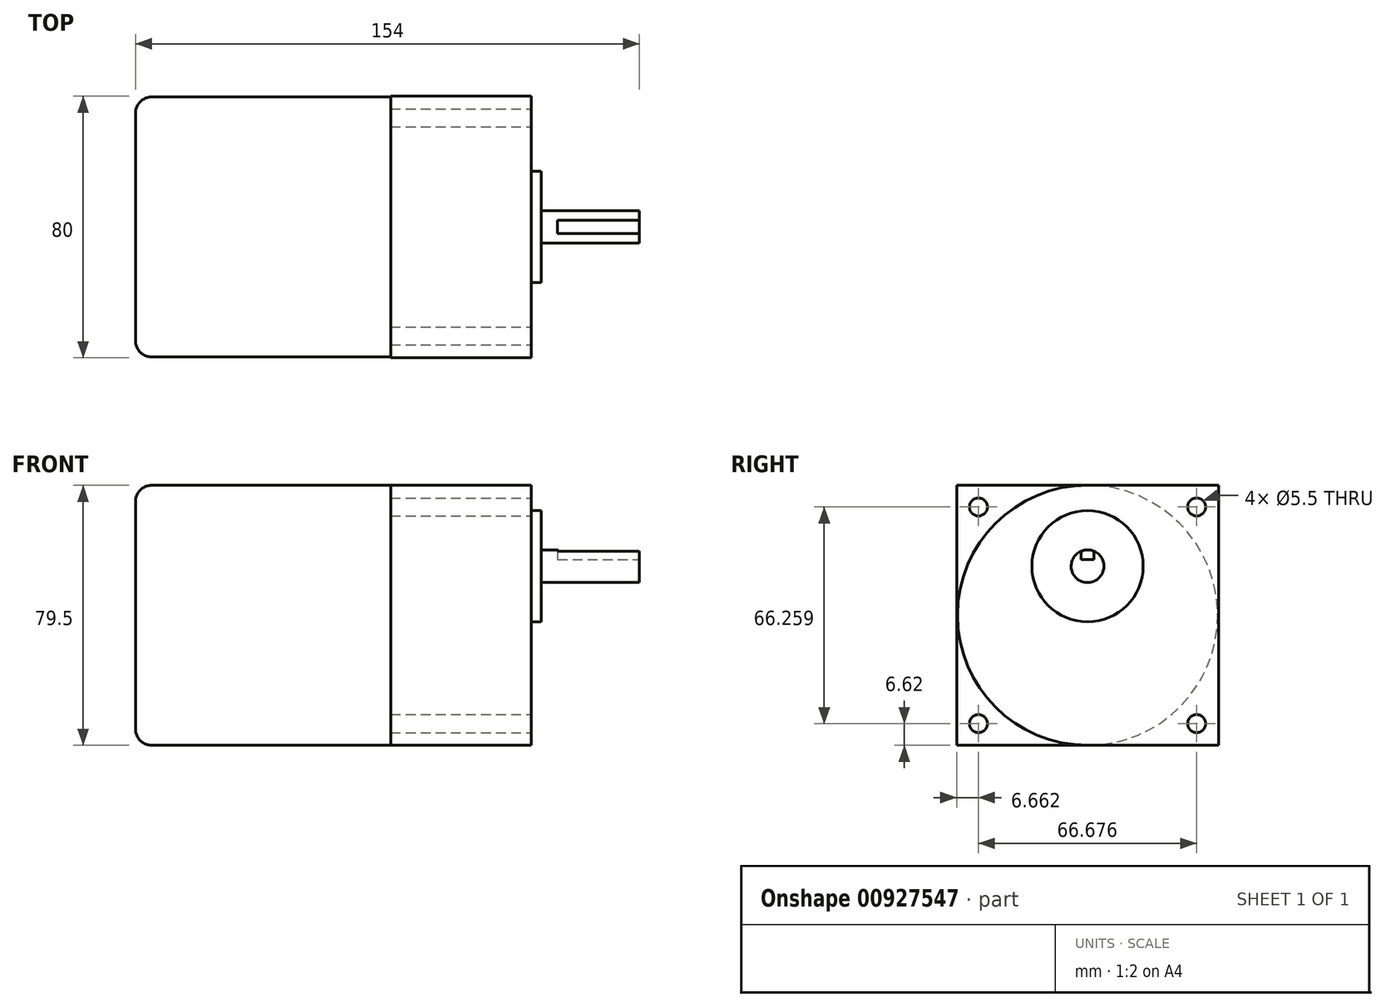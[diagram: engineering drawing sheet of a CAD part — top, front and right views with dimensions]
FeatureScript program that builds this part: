
annotation { "Feature Type Name" : "Feature", "Feature Type Description" : "" }
export const myFeature = defineFeature(function(context is Context, id is Id, definition is map)
    precondition{}
    {
        {
            var Q0;
            Q0=qCreatedBy(makeId("Right.planeOp"),FACE);
            var sketch = newSketch(context, id + "F0", { "sketchPlane" : qUnion([Q0])});
            skLineSegment(sketch, "E0.bottom", {"start": v(40, 39.75) * mm, "end": v(-40, 39.75) * mm});
            skLineSegment(sketch, "E0.top", {"start": v(40, -39.75) * mm, "end": v(-40, -39.75) * mm});
            skLineSegment(sketch, "E0.left", {"start": v(40, 39.75) * mm, "end": v(40, -39.75) * mm});
            skLineSegment(sketch, "E0.right", {"start": v(-40, 39.75) * mm, "end": v(-40, -39.75) * mm});
            skPoint(sketch, "E0.middle", {"position": v(0, 0) * mm});
            skSolve(sketch);
        }
        {
            var Q0;
            Q0 = qSketchRegion(id + "F0", true);
            extrude(context, id + "F1", {"entities" : qUnion([Q0]), "oppositeDirection" : true, "depth" : (9 + 34) * mm, "offsetDistance" : 25 * mm});
        }
        {
            var Q0;
            Q0=makeQuery(id+"F1.opExtrude","CAP_FACE",FACE,{"disambiguationData":[OSD([sQuery(id+"F0.wireOp",EDGE,"E0.bottom"),sQuery(id+"F0.wireOp",EDGE,"E0.top"),sQuery(id+"F0.wireOp",EDGE,"E0.left"),sQuery(id+"F0.wireOp",EDGE,"E0.right")])],"isStart":false});
            var sketch = newSketch(context, id + "F2", { "sketchPlane" : qUnion([Q0])});
            skCircle(sketch, "E1", {"center": v(0, 0) * mm, "radius": 39.75 * mm});
            skSolve(sketch);
        }
        {
            var Q0;
            {var subQ0=sQuery(id+"F2.wireOp",EDGE,"E1");var subQ1=makeQuery(id+"F2.imprint","INTERSECT",VERTEX,{"derivedFrom":[makeQuery(id+"F1.opExtrude","CAP_EDGE",EDGE,{"disambiguationData":[OSD([sQuery(id+"F0.wireOp",EDGE,"E0.bottom")])],"isStart":false}),subQ0]});Q0=makeQuery(id+"F2.imprint","IMPRINT",FACE,{"disambiguationData":[TD([[makeQuery(id+"F2.imprint","IMPRINT",EDGE,{"disambiguationData":[TD([[subQ1,-1.0]])],"derivedFrom":subQ0}),1.0]])]});}
            extrude(context, id + "F3", {"entities" : qUnion([Q0]), "operationType" : NewBodyOperationType.ADD, "depth" : 78 * mm, "offsetDistance" : 25 * mm});
        }
        {
            var Q0;
            Q0=makeQuery(id+"F3.opExtrude","CAP_EDGE",EDGE,{"disambiguationData":[OSD([sQuery(id+"F2.wireOp",EDGE,"E1")])],"isStart":false});
            fillet(context, id + "F4", {"entities" : qUnion([Q0]), "radius" : 5 * mm, "tangentPropagation" : true, "allowEdgeOverflow" : false});
        }
        {
            var Q0;
            Q0=makeQuery(id+"F1.opExtrude","CAP_FACE",FACE,{"disambiguationData":[OSD([sQuery(id+"F0.wireOp",EDGE,"E0.bottom"),sQuery(id+"F0.wireOp",EDGE,"E0.top"),sQuery(id+"F0.wireOp",EDGE,"E0.left"),sQuery(id+"F0.wireOp",EDGE,"E0.right")])],"isStart":true});
            var sketch = newSketch(context, id + "F5", { "sketchPlane" : qUnion([Q0])});
            skCircle(sketch, "E2", {"center": v(0, 0) * mm, "radius": 36.5 * mm});
            skLineSegment(sketch, "E3", {"start": v(-56.5, 0) * mm, "end": v(79.88, 0) * mm, "construction": true});
            skCircle(sketch, "E4", {"center": v(0, 15) * mm, "radius": 17 * mm});
            skSolve(sketch);
        }
        {
            var Q0;
            Q0=makeQuery(id+"F5.imprint","IMPRINT",FACE,{"disambiguationData":[TD([[makeQuery(id+"F5.imprint","IMPRINT",EDGE,{"derivedFrom":sQuery(id+"F5.wireOp",EDGE,"E4")}),1.0]])]});
            extrude(context, id + "F6", {"entities" : qUnion([Q0]), "operationType" : NewBodyOperationType.ADD, "depth" : 3 * mm, "offsetDistance" : 25 * mm});
        }
        {
            var Q0;
            Q0=makeQuery(id+"F1.opExtrude","CAP_FACE",FACE,{"disambiguationData":[OSD([sQuery(id+"F0.wireOp",EDGE,"E0.bottom"),sQuery(id+"F0.wireOp",EDGE,"E0.top"),sQuery(id+"F0.wireOp",EDGE,"E0.left"),sQuery(id+"F0.wireOp",EDGE,"E0.right")])],"isStart":true});
            var sketch = newSketch(context, id + "F7", { "sketchPlane" : qUnion([Q0])});
            skLineSegment(sketch, "E5", {"start": v(-40, 39.75) * mm, "end": v(40, -39.75) * mm, "construction": true});
            skLineSegment(sketch, "E6", {"start": v(-40, -39.75) * mm, "end": v(40, 39.75) * mm, "construction": true});
            skCircle(sketch, "E7", {"center": v(0, 0) * mm, "radius": 47 * mm, "construction": true});
            skPoint(sketch, "E8", {"position": v(-33.34, 33.13) * mm});
            skCircle(sketch, "E9", {"center": v(-33.34, 33.13) * mm, "radius": 2.75 * mm});
            skCircle(sketch, "E10.MirrorC", {"center": v(33.34, 33.13) * mm, "radius": 2.75 * mm});
            skCircle(sketch, "E11.MirrorC", {"center": v(-33.34, -33.13) * mm, "radius": 2.75 * mm});
            skCircle(sketch, "E12.MirrorC", {"center": v(33.34, -33.13) * mm, "radius": 2.75 * mm});
            skSolve(sketch);
        }
        {
            var Q0;
            Q0 = qSketchRegion(id + "F7", true);
            extrude(context, id + "F8", {"entities" : qUnion([Q0]), "operationType" : NewBodyOperationType.REMOVE, "endBound" : BoundingType.THROUGH_ALL, "oppositeDirection" : true, "depth" : 25 * mm, "offsetDistance" : 25 * mm});
        }
        {
            var Q0;
            Q0=makeQuery(id+"F6.opExtrude","CAP_FACE",FACE,{"disambiguationData":[OSD([sQuery(id+"F5.wireOp",EDGE,"E4")])],"isStart":false});
            var sketch = newSketch(context, id + "F9", { "sketchPlane" : qUnion([Q0])});
            skCircle(sketch, "E13", {"center": v(0, 15) * mm, "radius": 5 * mm});
            skSolve(sketch);
        }
        {
            var Q0;
            Q0 = qSketchRegion(id + "F9", true);
            extrude(context, id + "F10", {"entities" : qUnion([Q0]), "operationType" : NewBodyOperationType.ADD, "depth" : 30 * mm, "offsetDistance" : 25 * mm});
        }
        {
            var Q0;
            Q0=makeQuery(id+"F10.opExtrude","CAP_FACE",FACE,{"disambiguationData":[OSD([sQuery(id+"F9.wireOp",EDGE,"E13")])],"isStart":false});
            var sketch = newSketch(context, id + "F11", { "sketchPlane" : qUnion([Q0])});
            skLineSegment(sketch, "E14", {"start": v(2, 19.58) * mm, "end": v(2, 17.08) * mm});
            skLineSegment(sketch, "E15", {"start": v(2, 17.08) * mm, "end": v(0, 17.08) * mm});
            skLineSegment(sketch, "E16.MirrorCS", {"start": v(-2, 19.58) * mm, "end": v(-2, 17.08) * mm});
            skLineSegment(sketch, "E17.MirrorCS", {"start": v(-2, 17.08) * mm, "end": v(0, 17.08) * mm});
            skSolve(sketch);
        }
        {
            var Q0;
            {var subQ1=sQuery(id+"F11.wireOp",EDGE,"E14");Q0=makeQuery(id+"F11.imprint","IMPRINT",FACE,{"disambiguationData":[TD([[makeQuery(id+"F11.imprint","IMPRINT",EDGE,{"derivedFrom":subQ1}),-1.0]])]});}
            extrude(context, id + "F12", {"entities" : qUnion([Q0]), "operationType" : NewBodyOperationType.REMOVE, "oppositeDirection" : true, "depth" : 25 * mm, "offsetDistance" : 25 * mm});
        }
    });
